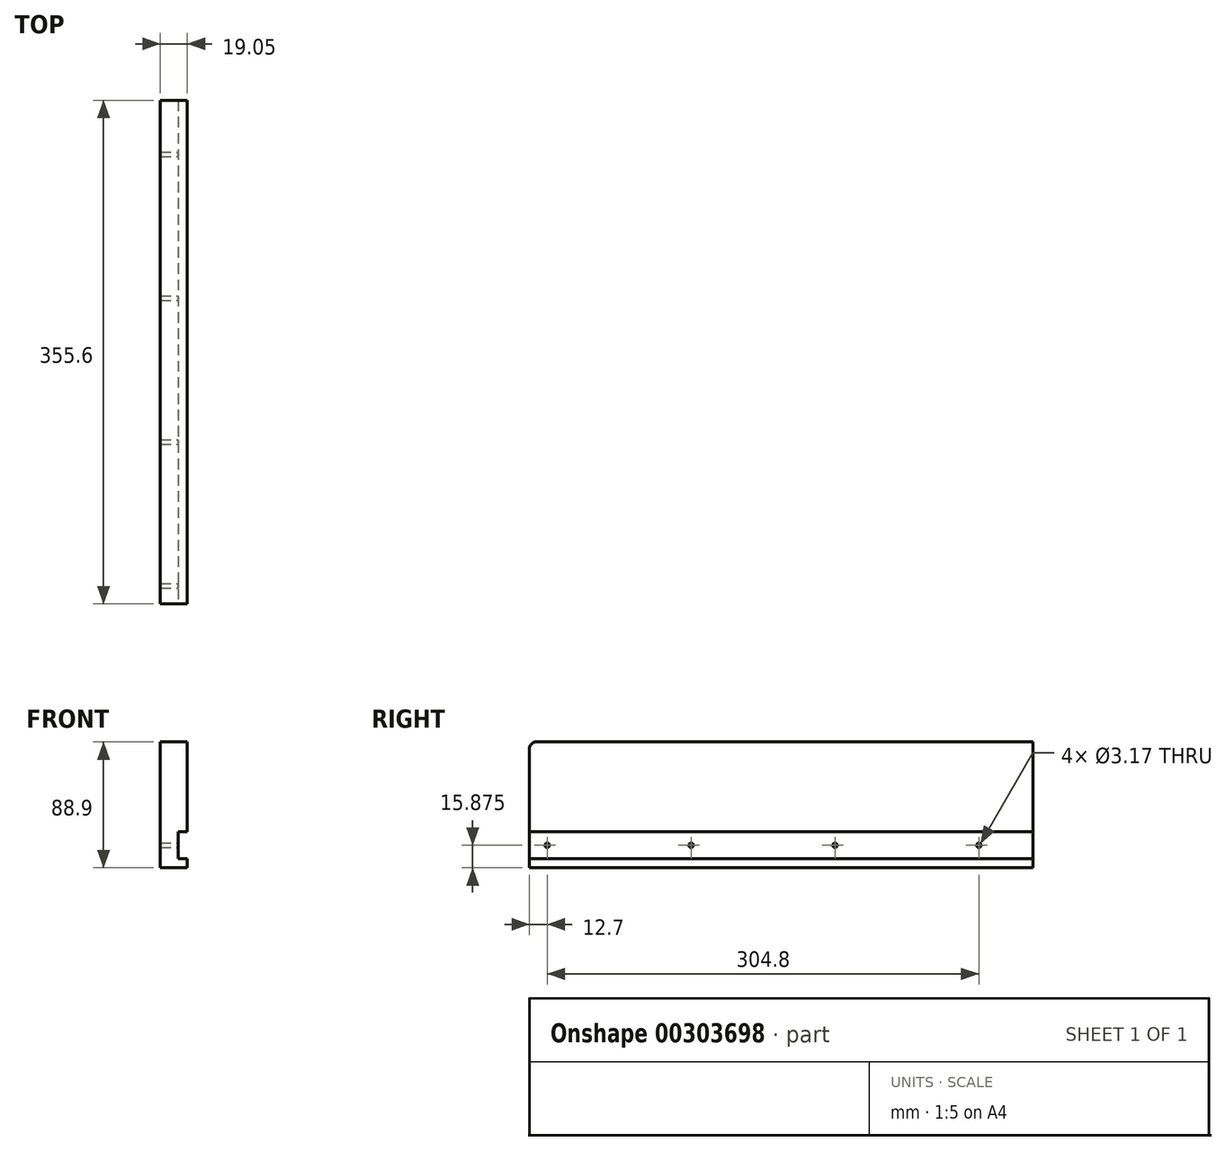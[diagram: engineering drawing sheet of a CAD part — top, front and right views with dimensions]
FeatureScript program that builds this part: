
annotation { "Feature Type Name" : "Feature", "Feature Type Description" : "" }
export const myFeature = defineFeature(function(context is Context, id is Id, definition is map)
    precondition{}
    {
        {
            var Q0;
            Q0=qCreatedBy(makeId("Right.planeOp"),FACE);
            var sketch = newSketch(context, id + "F0", { "sketchPlane" : qUnion([Q0])});
            skLineSegment(sketch, "E0.bottom", {"start": v(0, 0) * mm, "end": v(355.6, 0) * mm});
            skLineSegment(sketch, "E0.top", {"start": v(0, -88.9) * mm, "end": v(355.6, -88.9) * mm});
            skLineSegment(sketch, "E0.left", {"start": v(0, 0) * mm, "end": v(0, -88.9) * mm});
            skLineSegment(sketch, "E0.right", {"start": v(355.6, 0) * mm, "end": v(355.6, -88.9) * mm});
            skSolve(sketch);
        }
        {
            var Q0;
            Q0=qSketchRegion(id+"F0",true);
            extrude(context, id + "F1", {"entities" : qUnion([Q0]), "oppositeDirection" : true, "depth" : 19.05 * mm});
        }
        {
            var Q0;
            Q0=qCreatedBy(makeId("Right.planeOp"),FACE);
            var sketch = newSketch(context, id + "F2", { "sketchPlane" : qUnion([Q0])});
            skLineSegment(sketch, "E1.bottom", {"start": v(355.6, -82.55) * mm, "end": v(0, -82.55) * mm});
            skLineSegment(sketch, "E1.top", {"start": v(355.6, -63.5) * mm, "end": v(0, -63.5) * mm});
            skLineSegment(sketch, "E1.left", {"start": v(355.6, -82.55) * mm, "end": v(355.6, -63.5) * mm});
            skLineSegment(sketch, "E1.right", {"start": v(0, -82.55) * mm, "end": v(0, -63.5) * mm});
            skPoint(sketch, "E1.middle", {"position": v(177.8, -73.02) * mm});
            skSolve(sketch);
        }
        {
            var Q0;
            Q0=qSketchRegion(id+"F2",true);
            extrude(context, id + "F3", {"entities" : qUnion([Q0]), "operationType" : NewBodyOperationType.REMOVE, "oppositeDirection" : true, "depth" : 6.35 * mm});
        }
        {
            var Q0;
            Q0=makeQuery(id+"F1.opExtrude","SWEPT_EDGE",EDGE,{"disambiguationData":[OSD([sQuery(id+"F0.wireOp",EDGE,"E0.bottom"),sQuery(id+"F0.wireOp",EDGE,"E0.left")])]});
            fillet(context, id + "F4", {"entities" : qUnion([Q0]), "radius" : 5.08 * mm, "tangentPropagation" : true, "allowEdgeOverflow" : false});
        }
        {
            var Q0;
            Q0=qCreatedBy(makeId("Right.planeOp"),FACE);
            var sketch = newSketch(context, id + "F5", { "sketchPlane" : qUnion([Q0])});
            skCircle(sketch, "E2", {"center": v(12.7, -73.03) * mm, "radius": 1.59 * mm});
            skCircle(sketch, "E3.1.0.0", {"center": v(114.3, -73.03) * mm, "radius": 1.59 * mm});
            skCircle(sketch, "E3.2.0.0", {"center": v(215.9, -73.03) * mm, "radius": 1.59 * mm});
            skCircle(sketch, "E3.3.0.0", {"center": v(317.5, -73.03) * mm, "radius": 1.59 * mm});
            skLineSegment(sketch, "E3.direction1", {"start": v(12.7, -73.03) * mm, "end": v(114.3, -73.03) * mm, "construction": true});
            skSolve(sketch);
        }
        {
            var Q0;
            Q0 = qSketchRegion(id + "F5", true);
            extrude(context, id + "F6", {"entities" : qUnion([Q0]), "operationType" : NewBodyOperationType.REMOVE, "endBound" : BoundingType.THROUGH_ALL, "oppositeDirection" : true, "depth" : 25.4 * mm});
        }
    });
